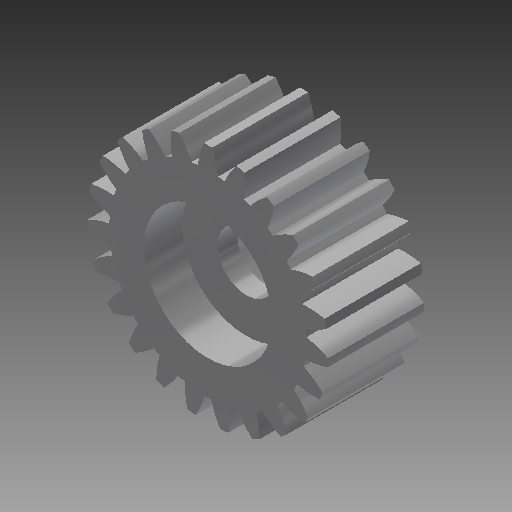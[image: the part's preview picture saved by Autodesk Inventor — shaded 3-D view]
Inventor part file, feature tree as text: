
AUTODESK INVENTOR PART (.ipt)
format: ipt  version: 2019 (Build 230136000, 136)  size: 290,304 bytes
history: native  units: mm (DEFAULTED — no unit token found)
features: sketch x5, extrude x4, plane x3, other x3
ambient origin geometry x8: Origin, YZ Plane, XZ Plane, XY Plane, X Axis, Y Axis, Z Axis, Center Point
bodies: Solid1 (feature_tree)
feature tree (15):
  extrude  "Extrusion1"  Depth=15.0mm TaperAngle=0.0deg
  plane  "Work Plane2"
  plane  "Work Plane8"
  plane  "Work Plane9"
  other  "正齒輪"
  extrude  "擠出7"  Depth=10.0mm TaperAngle=0.0deg
  extrude  "擠出8"  Depth=6.0mm
  extrude  "擠出9"  Depth=6.0mm TaperAngle=0.0deg
  sketch  "Sketch1"  dims[d0=37.5mm d1=15.0mm d2=0.0mm]
  sketch  "Sketch2"  dims[d3=34.5mm d4=10.0mm d5=0.0mm d16=60.0mm d17=0.0mm d34=1.36591mm d39=0.0mm d41=0.0mm d43=60.0mm d46=60.0mm d47=0.0mm d48=0.0mm d72=20.0mm d73=6.0mm d74=0.0mm d75=20.0mm d76=6.0mm d77=0.0mm d78=9.0mm d79=6.0mm d80=0.0mm]
  other  "Srf1"
  sketch  "草圖8"
  sketch  "草圖9"
  sketch  "草圖10"
  other  "節圓直徑"
